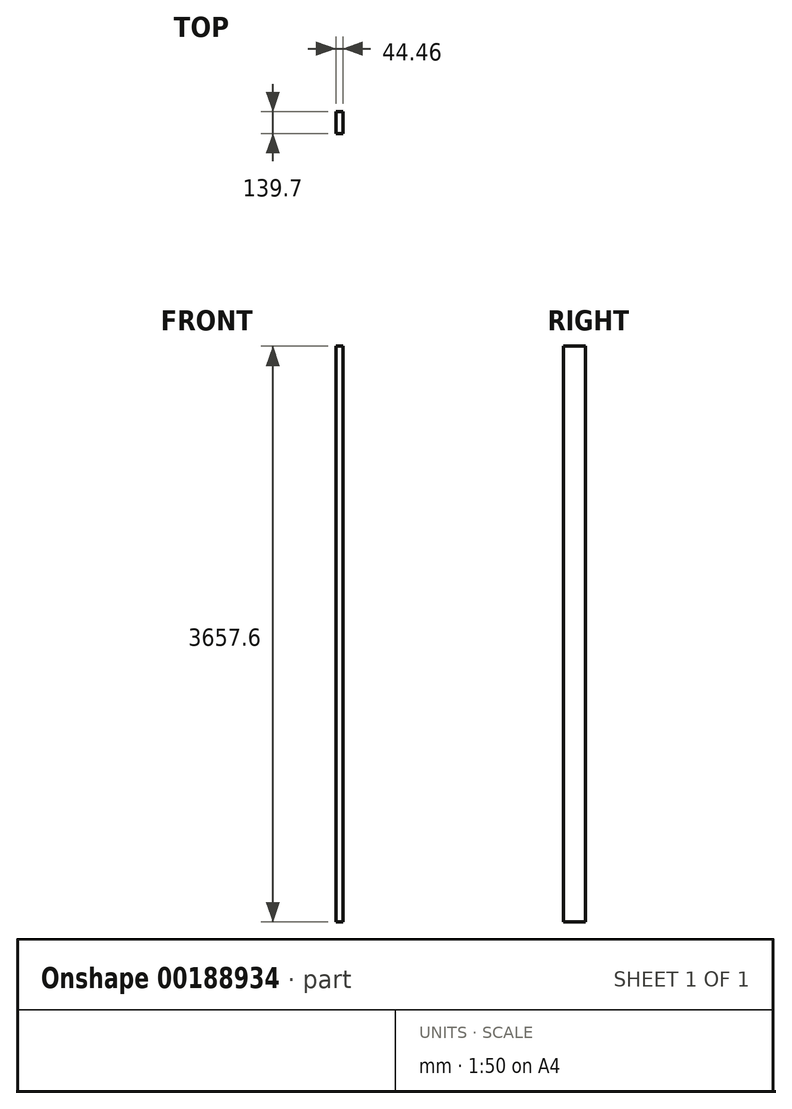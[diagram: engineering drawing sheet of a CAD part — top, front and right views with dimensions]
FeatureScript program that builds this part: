
annotation { "Feature Type Name" : "Feature", "Feature Type Description" : "" }
export const myFeature = defineFeature(function(context is Context, id is Id, definition is map)
    precondition{}
    {
        {
            var Q0;
            Q0=qCreatedBy(makeId("Top.planeOp"),FACE);
            var sketch = newSketch(context, id + "F1", { "sketchPlane" : qUnion([Q0])});
            skLineSegment(sketch, "E0.bottom", {"start": v(22.23, -69.85) * mm, "end": v(-22.22, -69.85) * mm});
            skLineSegment(sketch, "E0.top", {"start": v(22.22, 69.85) * mm, "end": v(-22.23, 69.85) * mm});
            skLineSegment(sketch, "E0.left", {"start": v(22.23, -69.85) * mm, "end": v(22.22, 69.85) * mm});
            skLineSegment(sketch, "E0.right", {"start": v(-22.22, -69.85) * mm, "end": v(-22.23, 69.85) * mm});
            skPoint(sketch, "E0.middle", {"position": v(0, 0) * mm});
            skSolve(sketch);
        }
        {
            var Q0;
            Q0=makeQuery(id+"F1.imprint","IMPRINT",FACE,{"disambiguationData":[TD([[makeQuery(id+"F1.imprint","IMPRINT",EDGE,{"derivedFrom":sQuery(id+"F1.wireOp",EDGE,"E0.bottom")}),-1.0]])]});
            extrude(context, id + "F0", {"entities" : qUnion([Q0]), "endBound" : BoundingType.SYMMETRIC, "depth" : 3657.6 * mm});
        }
    });
